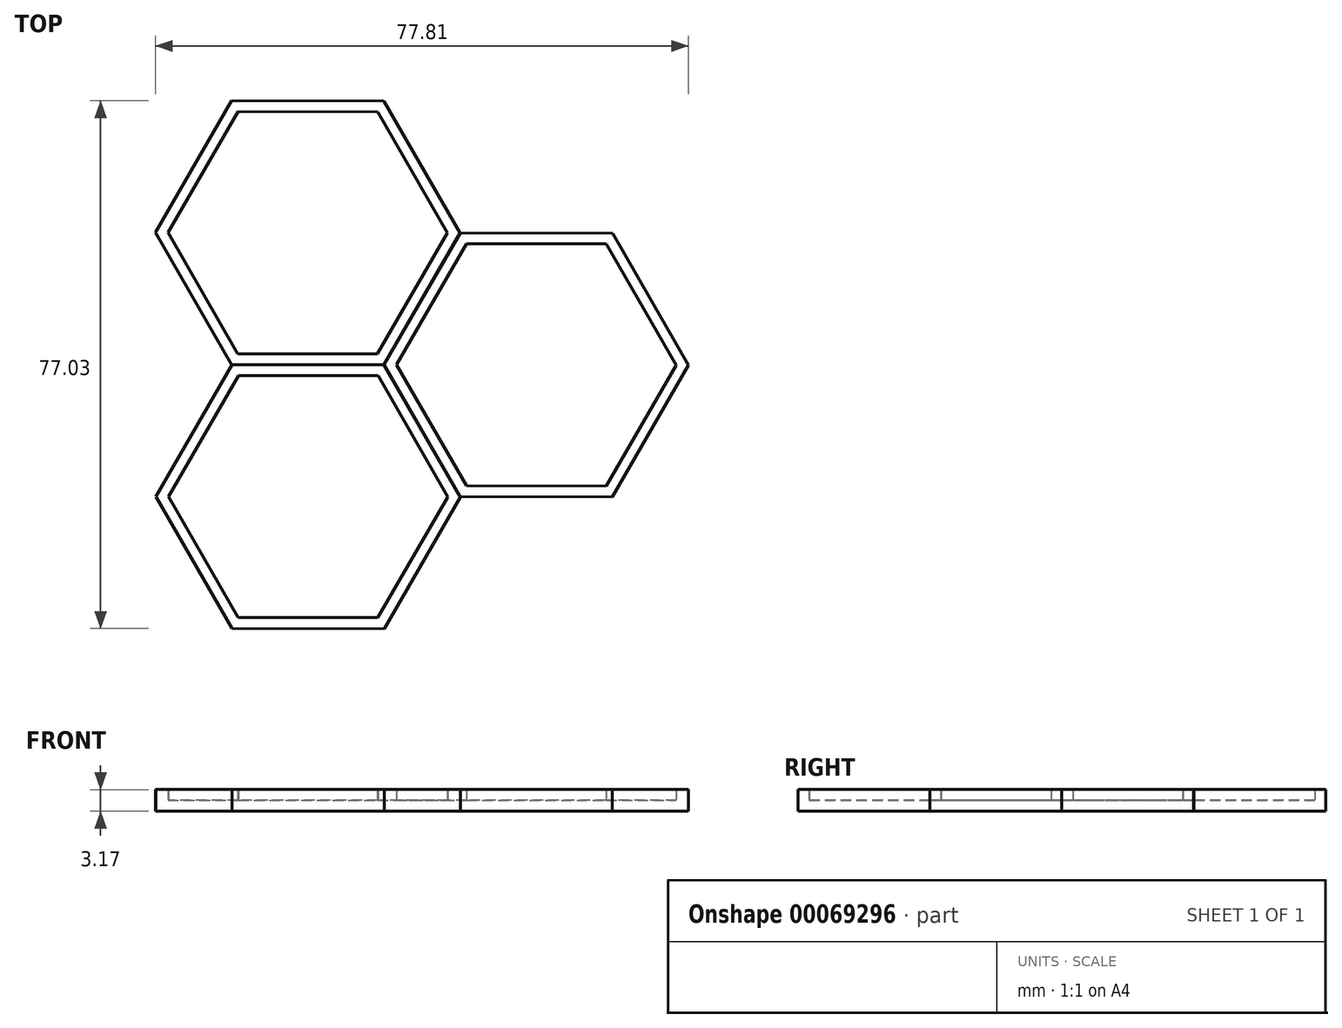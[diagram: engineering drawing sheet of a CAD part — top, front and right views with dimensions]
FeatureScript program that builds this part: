
annotation { "Feature Type Name" : "Feature", "Feature Type Description" : "" }
export const myFeature = defineFeature(function(context is Context, id is Id, definition is map)
    precondition{}
    {
        {
            var Q0;
            Q0=qCreatedBy(makeId("Top.planeOp"),FACE);
            var sketch = newSketch(context, id + "F0", { "sketchPlane" : qUnion([Q0])});
            skCircle(sketch, "E0.cCircle", {"center": v(0, 0) * mm, "radius": 19.25 * mm, "construction": true});
            skLineSegment(sketch, "E0.0", {"start": v(11.14, 19.23) * mm, "end": v(22.22, -0.03) * mm});
            skLineSegment(sketch, "E0.1", {"start": v(22.22, -0.03) * mm, "end": v(11.09, -19.26) * mm});
            skLineSegment(sketch, "E0.2", {"start": v(11.09, -19.26) * mm, "end": v(-11.14, -19.23) * mm});
            skLineSegment(sketch, "E0.3", {"start": v(-11.14, -19.23) * mm, "end": v(-22.22, 0.03) * mm});
            skLineSegment(sketch, "E0.4", {"start": v(-22.23, 0.03) * mm, "end": v(-11.09, 19.26) * mm});
            skLineSegment(sketch, "E0.5", {"start": v(-11.09, 19.26) * mm, "end": v(11.14, 19.23) * mm});
            skPoint(sketch, "E0.0.midPoint", {"position": v(16.68, 9.6) * mm});
            skSolve(sketch);
        }
        {
            var Q0;
            Q0=qSketchRegion(id+"F0",true);
            extrude(context, id + "F1", {"entities" : qUnion([Q0]), "depth" : 3.17 * mm});
        }
        {
            var Q0;
            Q0=makeQuery(id+"F1.opExtrude","CAP_FACE",FACE,{"disambiguationData":[OSD([sQuery(id+"F0.wireOp",EDGE,"E0.0"),sQuery(id+"F0.wireOp",EDGE,"E0.1"),sQuery(id+"F0.wireOp",EDGE,"E0.2"),sQuery(id+"F0.wireOp",EDGE,"E0.3"),sQuery(id+"F0.wireOp",EDGE,"E0.4"),sQuery(id+"F0.wireOp",EDGE,"E0.5")])],"isStart":false});
            shell(context, id + "F2", {"entities" : qUnion([Q0]), "thickness" : 1.59 * mm});
        }
        {
            var Q0;
            Q0=makeQuery(id+"F1.opExtrude","SWEPT_BODY",BODY,{"disambiguationData":[OSD([sQuery(id+"F0.wireOp",EDGE,"E0.0"),sQuery(id+"F0.wireOp",EDGE,"E0.1"),sQuery(id+"F0.wireOp",EDGE,"E0.2"),sQuery(id+"F0.wireOp",EDGE,"E0.3"),sQuery(id+"F0.wireOp",EDGE,"E0.4"),sQuery(id+"F0.wireOp",EDGE,"E0.5")])]});
            transform(context, id + "F3", {"entities" : qUnion([Q0]), "transformType" : TransformType.TRANSLATION_3D, "dx" : 33.36 * mm, "dy" : -19.29 * mm, "dz" : 0 * mm, "makeCopy" : true});
        }
        {
            var Q0;
            Q0=makeQuery(id+"F1.opExtrude","SWEPT_BODY",BODY,{"disambiguationData":[OSD([sQuery(id+"F0.wireOp",EDGE,"E0.0"),sQuery(id+"F0.wireOp",EDGE,"E0.1"),sQuery(id+"F0.wireOp",EDGE,"E0.2"),sQuery(id+"F0.wireOp",EDGE,"E0.3"),sQuery(id+"F0.wireOp",EDGE,"E0.4"),sQuery(id+"F0.wireOp",EDGE,"E0.5")])]});
            transform(context, id + "F4", {"entities" : qUnion([Q0]), "transformType" : TransformType.TRANSLATION_3D, "dx" : 0.05 * mm, "dy" : -38.5 * mm, "dz" : 0 * mm, "makeCopy" : true});
        }
    });
